# Revit family: Malvestio_320950
name_source: partatom
category: Furniture
revit_build: Autodesk Revit Architecture 2014 (Build: 20131024_2115(x64)
units: mm (PartAtom-declared; Revit-internal decimal feet)

## types (1)
- Malvestio_320950
    BIMobject category = Other Furniture
    Date of publishing = 2014-10-30
    Depth = 840 mm  [stored 2.75591 ft]
    Description = “oneday” 4-section electric stretcher for long hospital stays with adjustment system on 2 couples of compass-leverages, abs mattress sections, translating backrest, extendible mattress platform, electric trendelenburg and reverse-trendelenburg adjustments.
    Design country = Italy
    Edition number = 1
    Height = 800 mm  [stored 2.62467 ft]
    IFC Classification = Furniture
    Installation instructions = http://www.malvestio.it
    Manufacturer country = Italy
    Manufacturer name = Malvestio
    Manufacturer url = http://www.malvestio.it
    Material main = Plastic-Malvestio-320950-Laminated
    Material secondary = Stainless-Malvestio-320950-Steel
    Nominal height = 800
    Nominal width = 2180
    Product SKU = STRETCHERS-320950
    Product data url = http://www.malvestio.it
    QR code = http://malvestio.bimobject.com
    UNSPSC Code = 56
    UNSPSC Name = Furniture and Furnishings
    URL = http://malvestio.bimobject.com
    Weight Net (Kg) = 100
    Width = 2180 mm  [stored 7.15223 ft]
    Youtube clip = http://www.malvestio.it

note: [stored X ft] marks values corroborated as IEEE doubles in the binary element streams (Revit-internal decimal feet)

## geometry (parser evidence)
native form markers: Sweep x3
no freeform markers — native parametric forms only
